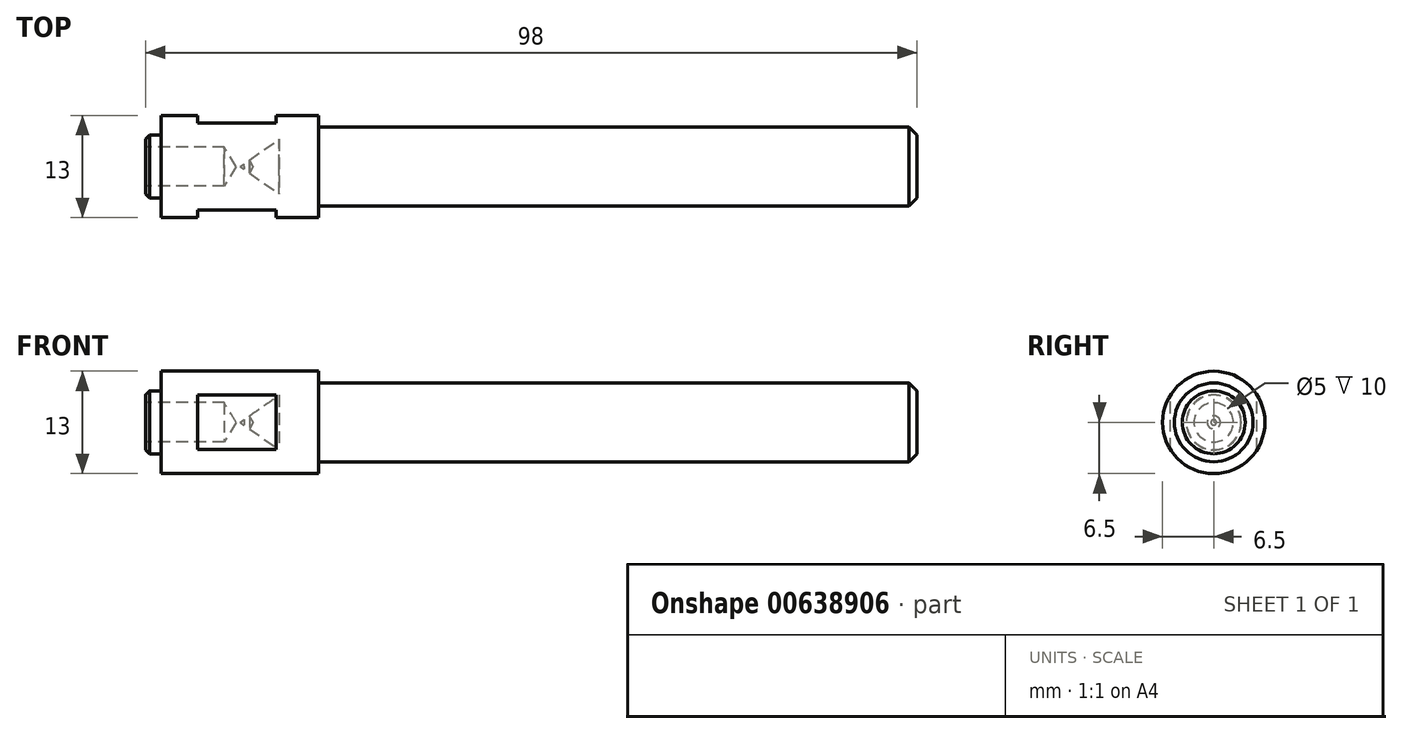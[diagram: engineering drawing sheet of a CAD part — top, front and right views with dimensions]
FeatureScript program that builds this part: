
annotation { "Feature Type Name" : "Feature", "Feature Type Description" : "" }
export const myFeature = defineFeature(function(context is Context, id is Id, definition is map)
    precondition{}
    {
        {
            var Q0;
            Q0=qCreatedBy(makeId("Front.planeOp"),FACE);
            var sketch = newSketch(context, id + "F0", { "sketchPlane" : qUnion([Q0])});
            skLineSegment(sketch, "E0", {"start": v(132.96, -3.46) * mm, "end": v(132.96, 3.46) * mm});
            skLineSegment(sketch, "E1", {"start": v(143.96, -3.46) * mm, "end": v(143.96, 3.46) * mm});
            skCircle(sketch, "E2", {"center": v(138.46, 0) * mm, "radius": 6.5 * mm});
            skLineSegment(sketch, "E3", {"start": v(131.46, 0) * mm, "end": v(145.46, 0) * mm});
            skLineSegment(sketch, "E4", {"start": v(138.46, -7) * mm, "end": v(138.46, 7) * mm});
            skCircle(sketch, "E5", {"center": v(138.46, 0) * mm, "radius": 5 * mm});
            skCircle(sketch, "E6", {"center": v(138.46, 0) * mm, "radius": 4 * mm});
            skLineSegment(sketch, "E7", {"start": v(-2, -3.5) * mm, "end": v(-2, 3.5) * mm});
            skLineSegment(sketch, "E8", {"start": v(-1.5, -4) * mm, "end": v(-1.5, 4) * mm});
            skLineSegment(sketch, "E9", {"start": v(95, 5) * mm, "end": v(20, 5) * mm});
            skLineSegment(sketch, "E10", {"start": v(20, -6.5) * mm, "end": v(20, 6.5) * mm});
            skLineSegment(sketch, "E11", {"start": v(-2, 2.06) * mm, "end": v(10.5, 2.06) * mm});
            skLineSegment(sketch, "E12", {"start": v(10.5, 2.06) * mm, "end": v(10.5, -2.06) * mm});
            skLineSegment(sketch, "E13", {"start": v(10.5, -2.06) * mm, "end": v(-2, -2.06) * mm});
            skLineSegment(sketch, "E14", {"start": v(10.5, -2.06) * mm, "end": v(11.7, 0) * mm});
            skLineSegment(sketch, "E15", {"start": v(10.5, 2.06) * mm, "end": v(11.7, 0) * mm});
            skLineSegment(sketch, "E16", {"start": v(8, 2.5) * mm, "end": v(8, -2.5) * mm});
            skLineSegment(sketch, "E17", {"start": v(8, -2.5) * mm, "end": v(-2, -2.5) * mm});
            skLineSegment(sketch, "E18", {"start": v(-2, 2.5) * mm, "end": v(8, 2.5) * mm});
            skLineSegment(sketch, "E19", {"start": v(8, -2.5) * mm, "end": v(8.75, -2.06) * mm});
            skLineSegment(sketch, "E20", {"start": v(8, 2.5) * mm, "end": v(8.75, 2.06) * mm});
            skLineSegment(sketch, "E21", {"start": v(13.06, 0) * mm, "end": v(-3.37, 0) * mm});
            skLineSegment(sketch, "E22", {"start": v(-1.5, -4) * mm, "end": v(0, -4) * mm});
            skLineSegment(sketch, "E23", {"start": v(-1.5, 4) * mm, "end": v(0, 4) * mm});
            skLineSegment(sketch, "E24", {"start": v(0, -6.5) * mm, "end": v(0, 6.5) * mm});
            skLineSegment(sketch, "E25", {"start": v(15, -3.46) * mm, "end": v(5, -3.46) * mm});
            skLineSegment(sketch, "E26", {"start": v(5, -3.46) * mm, "end": v(5, 3.46) * mm});
            skLineSegment(sketch, "E27", {"start": v(15, -3.46) * mm, "end": v(15, 3.46) * mm});
            skLineSegment(sketch, "E28", {"start": v(15, 3.46) * mm, "end": v(5, 3.46) * mm});
            skLineSegment(sketch, "E29", {"start": v(5, -3.46) * mm, "end": v(15, 3.46) * mm});
            skLineSegment(sketch, "E30", {"start": v(5, 3.46) * mm, "end": v(15, -3.46) * mm});
            skLineSegment(sketch, "E31", {"start": v(0, 6.5) * mm, "end": v(20, 6.5) * mm});
            skLineSegment(sketch, "E32", {"start": v(0, -6.5) * mm, "end": v(20, -6.5) * mm});
            skLineSegment(sketch, "E33", {"start": v(-1.5, 4) * mm, "end": v(-2, 3.5) * mm});
            skLineSegment(sketch, "E34", {"start": v(-2, -3.5) * mm, "end": v(-1.5, -4) * mm});
            skLineSegment(sketch, "E35", {"start": v(-2, 0) * mm, "end": v(99.5, 0) * mm});
            skLineSegment(sketch, "E36", {"start": v(96, -4) * mm, "end": v(95, -5) * mm});
            skLineSegment(sketch, "E37", {"start": v(96, 4) * mm, "end": v(95, 5) * mm});
            skLineSegment(sketch, "E38", {"start": v(96, -4) * mm, "end": v(96, 4) * mm});
            skLineSegment(sketch, "E39", {"start": v(95, 5) * mm, "end": v(95, -5) * mm});
            skLineSegment(sketch, "E40", {"start": v(95, -5) * mm, "end": v(20, -5) * mm});
            skSolve(sketch);
        }
        {
            var Q0;
            {var subQ0=sQuery(id+"F0.wireOp",EDGE,"E9");Q0=makeQuery(id+"F0.imprint","IMPRINT",FACE,{"disambiguationData":[TD([[makeQuery(id+"F0.imprint","IMPRINT",EDGE,{"derivedFrom":subQ0}),1.0]])]});}
            var Q1;
            {var subQ1=sQuery(id+"F0.wireOp",EDGE,"E11");var subQ5=sQuery(id+"F0.wireOp",EDGE,"E26");var subQ6=makeQuery(id+"F0.imprint","INTERSECT",VERTEX,{"derivedFrom":[subQ1,subQ5]});Q1=makeQuery(id+"F0.imprint","IMPRINT",FACE,{"disambiguationData":[TD([[makeQuery(id+"F0.imprint","IMPRINT",EDGE,{"disambiguationData":[TD([[subQ6,-1.0]])],"derivedFrom":subQ1}),-1.0]])]});}
            var Q2;
            {var subQ0=sQuery(id+"F0.wireOp",EDGE,"E23");Q2=makeQuery(id+"F0.imprint","IMPRINT",FACE,{"disambiguationData":[TD([[makeQuery(id+"F0.imprint","IMPRINT",EDGE,{"derivedFrom":subQ0}),-1.0]])]});}
            var Q3;
            {var subQ0=sQuery(id+"F0.wireOp",EDGE,"E35");var subQ3=makeQuery(id+"F0.imprint","IMPRINT",VERTEX,{"derivedFrom":subQ0});Q3=makeQuery(id+"F0.imprint","IMPRINT",FACE,{"disambiguationData":[TD([[makeQuery(id+"F0.imprint","IMPRINT",EDGE,{"disambiguationData":[TD([[subQ3,-1.0]])],"derivedFrom":subQ0}),1.0]])]});}
            var Q4;
            {var subQ5=sQuery(id+"F0.wireOp",EDGE,"E37");Q4=makeQuery(id+"F0.imprint","IMPRINT",FACE,{"disambiguationData":[TD([[makeQuery(id+"F0.imprint","IMPRINT",EDGE,{"derivedFrom":subQ5}),1.0]])]});}
            var Q5;
            {var subQ1=sQuery(id+"F0.wireOp",EDGE,"E12");var subQ3=sQuery(id+"F0.wireOp",EDGE,"E29");var subQ4=makeQuery(id+"F0.imprint","INTERSECT",VERTEX,{"derivedFrom":[subQ1,subQ3]});Q5=makeQuery(id+"F0.imprint","IMPRINT",FACE,{"disambiguationData":[TD([[makeQuery(id+"F0.imprint","IMPRINT",EDGE,{"disambiguationData":[TD([[subQ4,-1.0]])],"derivedFrom":subQ3}),1.0]])]});}
            var Q6;
            {var subQ0=sQuery(id+"F0.wireOp",EDGE,"E20");Q6=makeQuery(id+"F0.imprint","IMPRINT",FACE,{"disambiguationData":[TD([[makeQuery(id+"F0.imprint","IMPRINT",EDGE,{"derivedFrom":subQ0}),1.0]])]});}
            var Q7;
            {var subQ0=sQuery(id+"F0.wireOp",EDGE,"E24");var subQ1=sQuery(id+"F0.wireOp",EDGE,"E11");var subQ2=makeQuery(id+"F0.imprint","INTERSECT",VERTEX,{"derivedFrom":[subQ1,subQ0]});Q7=makeQuery(id+"F0.imprint","IMPRINT",FACE,{"disambiguationData":[TD([[makeQuery(id+"F0.imprint","IMPRINT",EDGE,{"disambiguationData":[TD([[subQ2,-1.0]])],"derivedFrom":subQ1}),-1.0]])]});}
            var Q8;
            {var subQ13=sQuery(id+"F0.wireOp",EDGE,"E28");Q8=makeQuery(id+"F0.imprint","IMPRINT",FACE,{"disambiguationData":[TD([[makeQuery(id+"F0.imprint","IMPRINT",EDGE,{"derivedFrom":subQ13}),-1.0]])]});}
            var Q9;
            {var subQ0=sQuery(id+"F0.wireOp",EDGE,"E35");var subQ1=sQuery(id+"F0.wireOp",EDGE,"E8");var subQ2=makeQuery(id+"F0.imprint","INTERSECT",VERTEX,{"derivedFrom":[subQ1,subQ0]});Q9=makeQuery(id+"F0.imprint","IMPRINT",FACE,{"disambiguationData":[TD([[makeQuery(id+"F0.imprint","IMPRINT",EDGE,{"disambiguationData":[TD([[subQ2,-1.0]])],"derivedFrom":subQ1}),-1.0]])]});}
            var Q10;
            {var subQ1=sQuery(id+"F0.wireOp",EDGE,"E11");var subQ9=makeQuery(id+"F0.imprint","INTERSECT",VERTEX,{"derivedFrom":[subQ1,sQuery(id+"F0.wireOp",EDGE,"E20")]});Q10=makeQuery(id+"F0.imprint","IMPRINT",FACE,{"disambiguationData":[TD([[makeQuery(id+"F0.imprint","IMPRINT",EDGE,{"disambiguationData":[TD([[subQ9,1.0]])],"derivedFrom":subQ1}),-1.0]])]});}
            var Q11;
            {var subQ0=sQuery(id+"F0.wireOp",EDGE,"E30");var subQ1=sQuery(id+"F0.wireOp",EDGE,"E11");var subQ2=makeQuery(id+"F0.imprint","INTERSECT",VERTEX,{"derivedFrom":[subQ1,subQ0]});Q11=makeQuery(id+"F0.imprint","IMPRINT",FACE,{"disambiguationData":[TD([[makeQuery(id+"F0.imprint","IMPRINT",EDGE,{"disambiguationData":[TD([[subQ2,-1.0]])],"derivedFrom":subQ1}),1.0]])]});}
            var Q12;
            {var subQ0=sQuery(id+"F0.wireOp",EDGE,"E29");var subQ1=sQuery(id+"F0.wireOp",EDGE,"E12");var subQ2=makeQuery(id+"F0.imprint","INTERSECT",VERTEX,{"derivedFrom":[subQ1,subQ0]});Q12=makeQuery(id+"F0.imprint","IMPRINT",FACE,{"disambiguationData":[TD([[makeQuery(id+"F0.imprint","IMPRINT",EDGE,{"disambiguationData":[TD([[subQ2,-1.0]])],"derivedFrom":subQ1}),1.0]])]});}
            var Q13;
            {var subQ0=sQuery(id+"F0.wireOp",EDGE,"E11");var subQ1=sQuery(id+"F0.wireOp",EDGE,"E7");var subQ2=makeQuery(id+"F0.imprint","INTERSECT",VERTEX,{"derivedFrom":[subQ1,subQ0]});Q13=makeQuery(id+"F0.imprint","IMPRINT",FACE,{"disambiguationData":[TD([[makeQuery(id+"F0.imprint","IMPRINT",EDGE,{"disambiguationData":[TD([[subQ2,1.0]])],"derivedFrom":subQ1}),-1.0]])]});}
            var Q14;
            {var subQ0=sQuery(id+"F0.wireOp",EDGE,"E30");var subQ1=sQuery(id+"F0.wireOp",EDGE,"E16");var subQ2=makeQuery(id+"F0.imprint","INTERSECT",VERTEX,{"derivedFrom":[subQ1,subQ0]});Q14=makeQuery(id+"F0.imprint","IMPRINT",FACE,{"disambiguationData":[TD([[makeQuery(id+"F0.imprint","IMPRINT",EDGE,{"disambiguationData":[TD([[subQ2,-1.0]])],"derivedFrom":subQ1}),1.0]])]});}
            var Q15;
            {var subQ0=sQuery(id+"F0.wireOp",EDGE,"E24");var subQ1=sQuery(id+"F0.wireOp",EDGE,"E11");var subQ2=makeQuery(id+"F0.imprint","INTERSECT",VERTEX,{"derivedFrom":[subQ1,subQ0]});Q15=makeQuery(id+"F0.imprint","IMPRINT",FACE,{"disambiguationData":[TD([[makeQuery(id+"F0.imprint","IMPRINT",EDGE,{"disambiguationData":[TD([[subQ2,-1.0]])],"derivedFrom":subQ1}),1.0]])]});}
            var Q16;
            {var subQ0=sQuery(id+"F0.wireOp",EDGE,"E26");var subQ1=sQuery(id+"F0.wireOp",EDGE,"E11");var subQ2=makeQuery(id+"F0.imprint","INTERSECT",VERTEX,{"derivedFrom":[subQ1,subQ0]});Q16=makeQuery(id+"F0.imprint","IMPRINT",FACE,{"disambiguationData":[TD([[makeQuery(id+"F0.imprint","IMPRINT",EDGE,{"disambiguationData":[TD([[subQ2,-1.0]])],"derivedFrom":subQ1}),1.0]])]});}
            var Q17;
            {var subQ0=sQuery(id+"F0.wireOp",EDGE,"E11");var subQ1=sQuery(id+"F0.wireOp",EDGE,"E8");var subQ2=makeQuery(id+"F0.imprint","INTERSECT",VERTEX,{"derivedFrom":[subQ1,subQ0]});Q17=makeQuery(id+"F0.imprint","IMPRINT",FACE,{"disambiguationData":[TD([[makeQuery(id+"F0.imprint","IMPRINT",EDGE,{"disambiguationData":[TD([[subQ2,-1.0]])],"derivedFrom":subQ1}),-1.0]])]});}
            var Q18;
            {var subQ0=sQuery(id+"F0.wireOp",EDGE,"E30");var subQ1=sQuery(id+"F0.wireOp",EDGE,"E11");var subQ2=makeQuery(id+"F0.imprint","INTERSECT",VERTEX,{"derivedFrom":[subQ1,subQ0]});Q18=makeQuery(id+"F0.imprint","IMPRINT",FACE,{"disambiguationData":[TD([[makeQuery(id+"F0.imprint","IMPRINT",EDGE,{"disambiguationData":[TD([[subQ2,-1.0]])],"derivedFrom":subQ1}),-1.0]])]});}
            var Q19;
            {var subQ0=sQuery(id+"F0.wireOp",EDGE,"E26");var subQ1=sQuery(id+"F0.wireOp",EDGE,"E18");var subQ2=makeQuery(id+"F0.imprint","INTERSECT",VERTEX,{"derivedFrom":[subQ1,subQ0]});Q19=makeQuery(id+"F0.imprint","IMPRINT",FACE,{"disambiguationData":[TD([[makeQuery(id+"F0.imprint","IMPRINT",EDGE,{"disambiguationData":[TD([[subQ2,-1.0]])],"derivedFrom":subQ1}),1.0]])]});}
            var Q20;
            {var subQ0=sQuery(id+"F0.wireOp",EDGE,"E33");Q20=makeQuery(id+"F0.imprint","IMPRINT",FACE,{"disambiguationData":[TD([[makeQuery(id+"F0.imprint","IMPRINT",EDGE,{"derivedFrom":subQ0}),1.0]])]});}
            var Q21;
            {var subQ0=sQuery(id+"F0.wireOp",EDGE,"E11");var subQ1=sQuery(id+"F0.wireOp",EDGE,"E7");var subQ2=makeQuery(id+"F0.imprint","INTERSECT",VERTEX,{"derivedFrom":[subQ1,subQ0]});Q21=makeQuery(id+"F0.imprint","IMPRINT",FACE,{"disambiguationData":[TD([[makeQuery(id+"F0.imprint","IMPRINT",EDGE,{"disambiguationData":[TD([[subQ2,-1.0]])],"derivedFrom":subQ1}),-1.0]])]});}
            var Q22;
            {var subQ0=sQuery(id+"F0.wireOp",EDGE,"E20");Q22=makeQuery(id+"F0.imprint","IMPRINT",FACE,{"disambiguationData":[TD([[makeQuery(id+"F0.imprint","IMPRINT",EDGE,{"derivedFrom":subQ0}),-1.0]])]});}
            var Q23;
            Q23=sQuery(id+"F0.wireOp",EDGE,"E35");
            revolve(context, id + "F1", {"entities" : qUnion([Q0, Q1, Q2, Q3, Q4, Q5, Q6, Q7, Q8, Q9, Q10, Q11, Q12, Q13, Q14, Q15, Q16, Q17, Q18, Q19, Q20, Q21, Q22]), "axis" : qUnion([Q23]), "revolveType" : RevolveType.FULL});
        }
        {
            var Q0;
            Q0=makeQuery(id+"F1.opRevolve","SWEPT_FACE",FACE,{"disambiguationData":[OSD([sQuery(id+"F0.wireOp",EDGE,"E7")])]});
            var sketch = newSketch(context, id + "F2", { "sketchPlane" : qUnion([Q0])});
            skCircle(sketch, "E41.0.0", {"center": v(0, 0) * mm, "radius": 3.5 * mm});
            skSolve(sketch);
        }
        {
            var Q0;
            Q0=sQuery(id+"F2.wireOp",VERTEX,"E41.0.0.center");
            var Q1;
            Q1=makeQuery(id+"F1.opRevolve","SWEPT_BODY",BODY,{"disambiguationData":[OSD([sQuery(id+"F0.wireOp",EDGE,"E7"),sQuery(id+"F0.wireOp",EDGE,"E9"),sQuery(id+"F0.wireOp",EDGE,"E10"),sQuery(id+"F0.wireOp",EDGE,"E12"),sQuery(id+"F0.wireOp",EDGE,"E23"),sQuery(id+"F0.wireOp",EDGE,"E24"),sQuery(id+"F0.wireOp",EDGE,"E29"),sQuery(id+"F0.wireOp",EDGE,"E31"),sQuery(id+"F0.wireOp",EDGE,"E33"),sQuery(id+"F0.wireOp",EDGE,"E35"),sQuery(id+"F0.wireOp",EDGE,"E37"),sQuery(id+"F0.wireOp",EDGE,"E38")])]});
            hole(context, id + "F3", {"style" : HoleStyle.SIMPLE, "endStyle" : HoleEndStyle.BLIND, "holeDiameter" : 5 * mm, "majorDiameter" : 5 * mm, "holeDepth" : 10 * mm, "isTappedThrough" : true, "tappedDepth" : 12 * mm, "tapClearance" : 3, "locations" : qUnion([Q0]), "scope" : qUnion([Q1])});
        }
        {
            var Q0;
            Q0=qCreatedBy(makeId("Top.planeOp"),FACE);
            var sketch = newSketch(context, id + "F4", { "sketchPlane" : qUnion([Q0])});
            skLineSegment(sketch, "E42", {"start": v(4.6, -5.5) * mm, "end": v(4.6, -29.77) * mm});
            skLineSegment(sketch, "E43.0", {"start": v(14.6, -5.5) * mm, "end": v(14.6, -29.77) * mm});
            skLineSegment(sketch, "E44", {"start": v(14.6, -29.77) * mm, "end": v(4.6, -29.77) * mm});
            skLineSegment(sketch, "E45", {"start": v(14.6, -5.5) * mm, "end": v(4.6, -5.5) * mm});
            skLineSegment(sketch, "E46.MirrorCS", {"start": v(14.6, 5.5) * mm, "end": v(14.6, 29.77) * mm});
            skLineSegment(sketch, "E47.MirrorCS", {"start": v(14.6, 29.77) * mm, "end": v(4.6, 29.77) * mm});
            skLineSegment(sketch, "E48.MirrorCS", {"start": v(4.6, 5.5) * mm, "end": v(4.6, 29.77) * mm});
            skLineSegment(sketch, "E49.MirrorCS", {"start": v(14.6, 5.5) * mm, "end": v(4.6, 5.5) * mm});
            skSolve(sketch);
        }
        {
            var Q0;
            Q0=makeQuery(id+"F4.imprint","IMPRINT",FACE,{"disambiguationData":[TD([[makeQuery(id+"F4.imprint","IMPRINT",EDGE,{"derivedFrom":sQuery(id+"F4.wireOp",EDGE,"E42")}),1.0]])]});
            var Q1;
            Q1=makeQuery(id+"F4.imprint","IMPRINT",FACE,{"disambiguationData":[TD([[makeQuery(id+"F4.imprint","IMPRINT",EDGE,{"derivedFrom":sQuery(id+"F4.wireOp",EDGE,"E46.MirrorCS")}),1.0]])]});
            extrude(context, id + "F5", {"entities" : qUnion([Q0, Q1]), "operationType" : NewBodyOperationType.REMOVE, "endBound" : BoundingType.SYMMETRIC, "oppositeDirection" : true, "depth" : 25 * mm, "offsetDistance" : 25 * mm});
        }
    });
